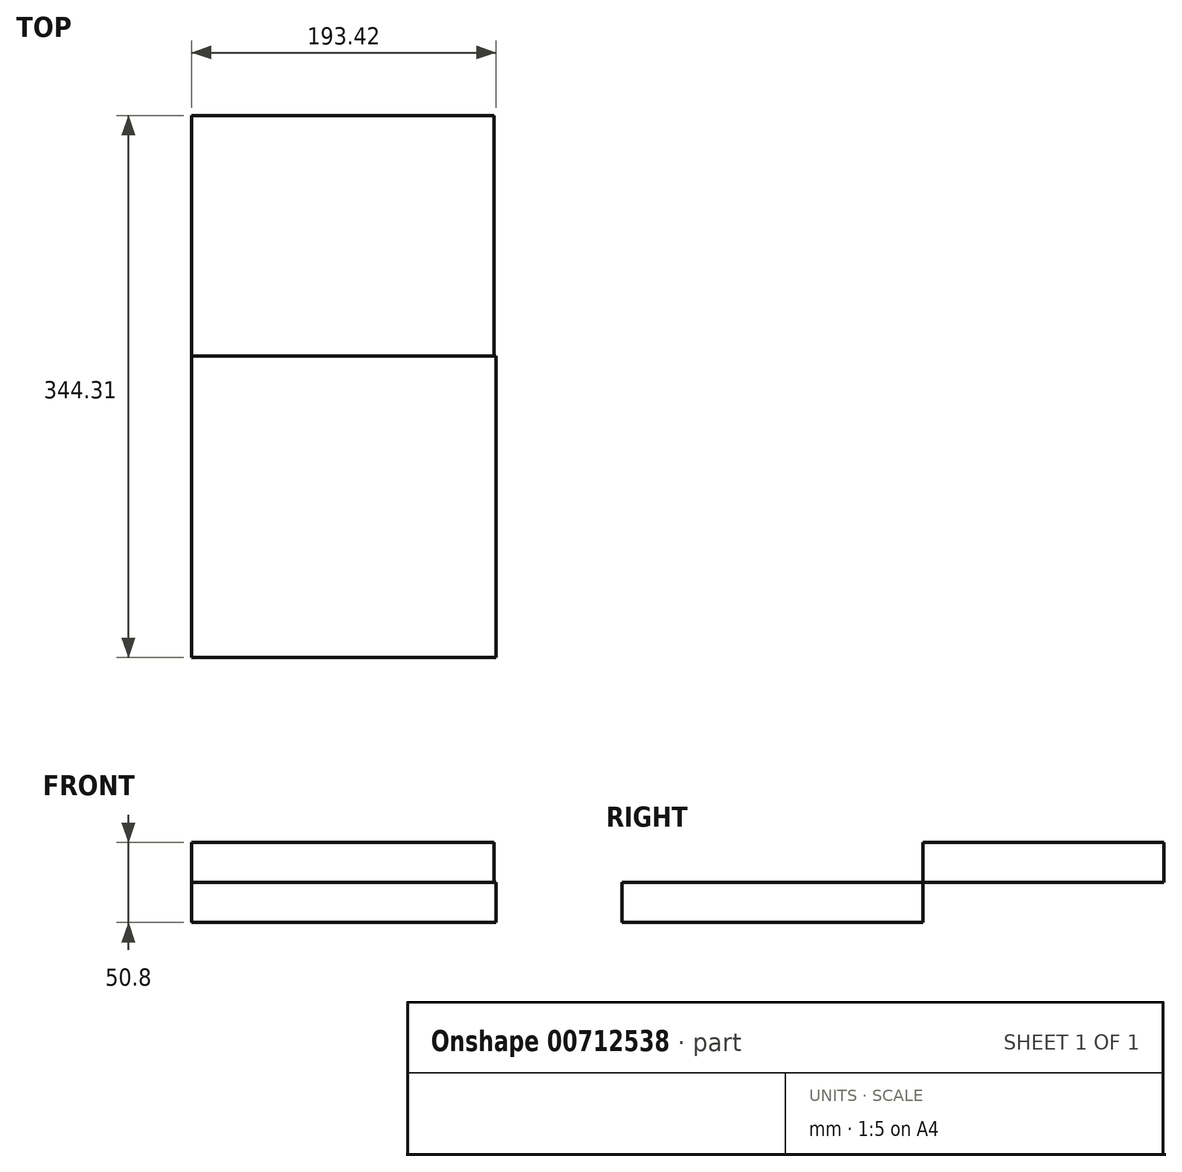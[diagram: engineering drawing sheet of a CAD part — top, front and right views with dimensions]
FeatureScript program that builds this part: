
annotation { "Feature Type Name" : "Feature", "Feature Type Description" : "" }
export const myFeature = defineFeature(function(context is Context, id is Id, definition is map)
    precondition{}
    {
        {
            var Q0;
            Q0=qCreatedBy(makeId("Top.planeOp"),FACE);
            var sketch = newSketch(context, id + "F0", { "sketchPlane" : qUnion([Q0])});
            skLineSegment(sketch, "E0.bottom", {"start": v(0, 0) * mm, "end": v(96.21, 0) * mm});
            skLineSegment(sketch, "E0.top", {"start": v(0, -191.33) * mm, "end": v(96.21, -191.33) * mm});
            skLineSegment(sketch, "E0.left", {"start": v(0, 0) * mm, "end": v(0, -191.33) * mm});
            skLineSegment(sketch, "E0.right", {"start": v(96.21, 0) * mm, "end": v(96.21, -191.33) * mm});
            skLineSegment(sketch, "E1.bottom", {"start": v(0, -191.33) * mm, "end": v(-41.45, -191.33) * mm});
            skLineSegment(sketch, "E1.top", {"start": v(0, -191.33) * mm, "end": v(-41.45, -191.33) * mm});
            skLineSegment(sketch, "E1.left", {"start": v(0, -191.33) * mm, "end": v(0, -191.33) * mm});
            skLineSegment(sketch, "E1.right", {"start": v(-41.45, -191.33) * mm, "end": v(-41.45, -191.33) * mm});
            skLineSegment(sketch, "E2.bottom", {"start": v(-41.45, -191.33) * mm, "end": v(-97.2, -191.33) * mm});
            skLineSegment(sketch, "E2.top", {"start": v(-41.45, -97.92) * mm, "end": v(-97.2, -97.92) * mm});
            skLineSegment(sketch, "E2.left", {"start": v(-41.45, -191.33) * mm, "end": v(-41.45, -97.92) * mm});
            skLineSegment(sketch, "E2.right", {"start": v(-97.2, -191.33) * mm, "end": v(-97.2, -97.92) * mm});
            skLineSegment(sketch, "E3.bottom", {"start": v(-41.45, -97.92) * mm, "end": v(0, -97.92) * mm});
            skLineSegment(sketch, "E3.top", {"start": v(-41.45, 0) * mm, "end": v(0, 0) * mm});
            skLineSegment(sketch, "E3.left", {"start": v(-41.45, -97.92) * mm, "end": v(-41.45, 0) * mm});
            skLineSegment(sketch, "E3.right", {"start": v(0, -97.92) * mm, "end": v(0, 0) * mm});
            skLineSegment(sketch, "E4.bottom", {"start": v(-41.45, 0) * mm, "end": v(-97.2, 0) * mm});
            skLineSegment(sketch, "E4.left", {"start": v(-41.45, 0) * mm, "end": v(-41.45, -97.92) * mm});
            skLineSegment(sketch, "E4.right", {"start": v(-97.2, 0) * mm, "end": v(-97.2, -97.92) * mm});
            skLineSegment(sketch, "E5.bottom", {"start": v(96.21, 0) * mm, "end": v(48.1, 0) * mm});
            skLineSegment(sketch, "E5.top", {"start": v(96.21, 0) * mm, "end": v(48.1, 0) * mm});
            skLineSegment(sketch, "E5.left", {"start": v(96.21, 0) * mm, "end": v(96.21, 0) * mm});
            skLineSegment(sketch, "E5.right", {"start": v(48.1, 0) * mm, "end": v(48.1, 0) * mm});
            skSolve(sketch);
        }
        {
            var Q0;
            Q0 = qSketchRegion(id + "F0", true);
            extrude(context, id + "F1", {"entities" : qUnion([Q0]), "depth" : 25.4 * mm, "offsetDistance" : 25.4 * mm});
        }
        {
            var Q0;
            Q0=makeQuery(id+"F1.opExtrude","CAP_FACE",FACE,{"disambiguationData":[OSD([sQuery(id+"F0.wireOp",EDGE,"E0.bottom"),sQuery(id+"F0.wireOp",EDGE,"E0.top"),sQuery(id+"F0.wireOp",EDGE,"E0.right"),sQuery(id+"F0.wireOp",EDGE,"E1.top"),sQuery(id+"F0.wireOp",EDGE,"E2.bottom"),sQuery(id+"F0.wireOp",EDGE,"E2.right"),sQuery(id+"F0.wireOp",EDGE,"E3.top"),sQuery(id+"F0.wireOp",EDGE,"E4.bottom"),sQuery(id+"F0.wireOp",EDGE,"E4.right"),sQuery(id+"F0.wireOp",EDGE,"E5.top")])],"isStart":false});
            var sketch = newSketch(context, id + "F2", { "sketchPlane" : qUnion([Q0])});
            skLineSegment(sketch, "E6.bottom", {"start": v(-97.2, 0) * mm, "end": v(96.21, 0) * mm});
            skLineSegment(sketch, "E6.top", {"start": v(-97.2, 0) * mm, "end": v(96.21, 0) * mm});
            skLineSegment(sketch, "E6.left", {"start": v(-97.2, 0) * mm, "end": v(-97.2, 0) * mm});
            skLineSegment(sketch, "E6.right", {"start": v(96.21, 0) * mm, "end": v(96.21, 0) * mm});
            skLineSegment(sketch, "E7.bottom", {"start": v(-97.2, 0) * mm, "end": v(95.03, 0) * mm});
            skLineSegment(sketch, "E7.top", {"start": v(-97.2, 152.98) * mm, "end": v(95.03, 152.98) * mm});
            skLineSegment(sketch, "E7.left", {"start": v(-97.2, 0) * mm, "end": v(-97.2, 152.98) * mm});
            skLineSegment(sketch, "E7.right", {"start": v(95.03, 0) * mm, "end": v(95.03, 152.98) * mm});
            skSolve(sketch);
        }
        {
            var Q0;
            Q0 = qSketchRegion(id + "F2", true);
            extrude(context, id + "F3", {"entities" : qUnion([Q0]), "depth" : 25.4 * mm, "offsetDistance" : 25.4 * mm});
        }
    });
